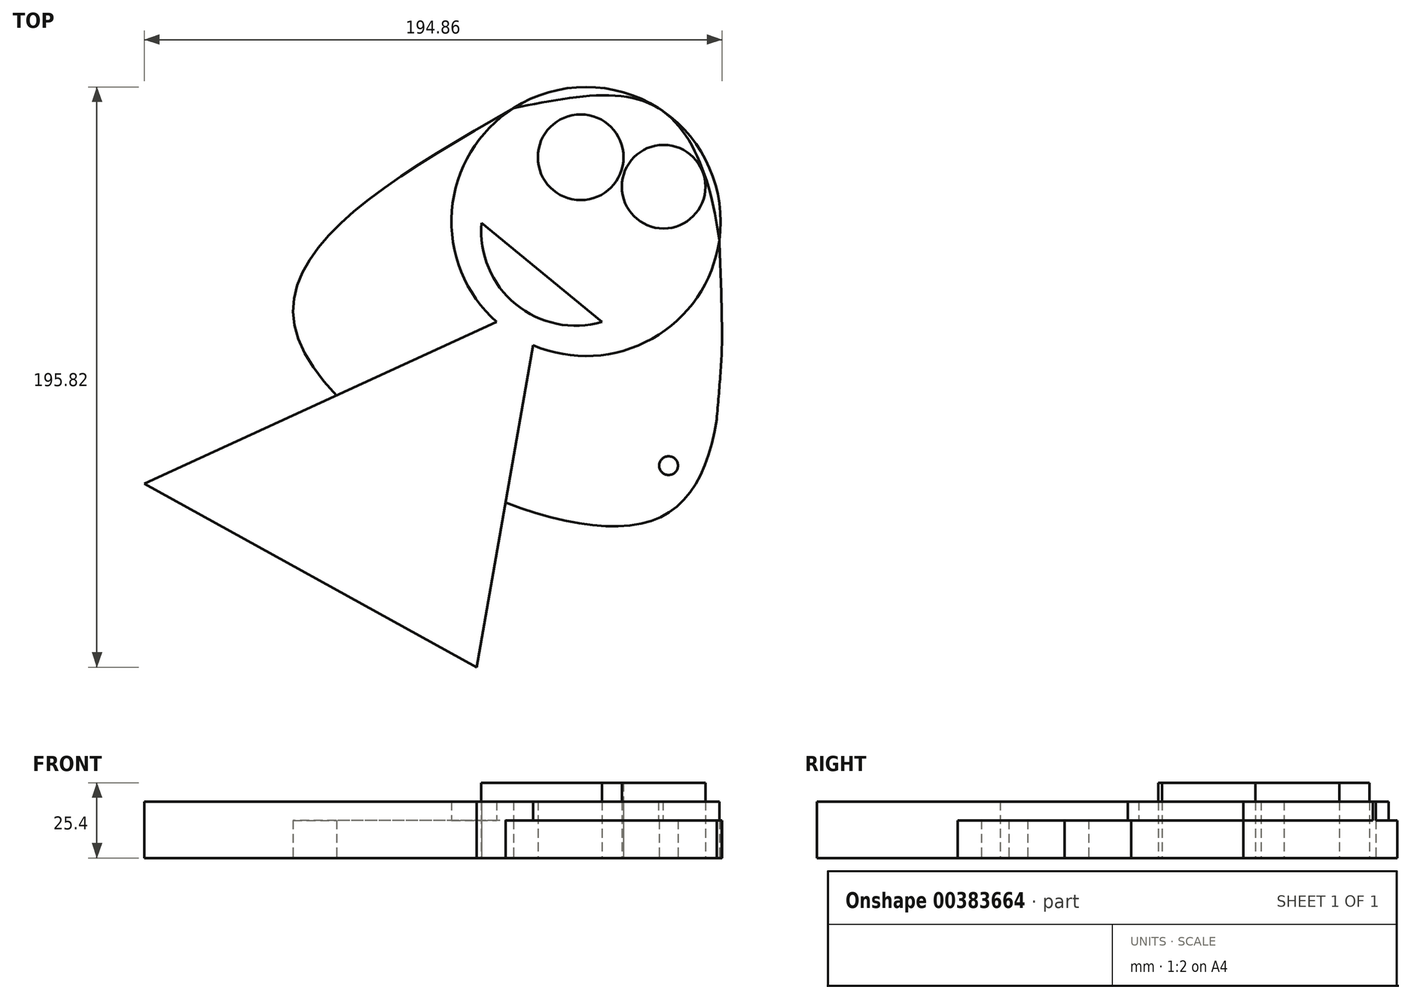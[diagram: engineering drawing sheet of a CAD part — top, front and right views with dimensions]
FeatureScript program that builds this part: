
annotation { "Feature Type Name" : "Feature", "Feature Type Description" : "" }
export const myFeature = defineFeature(function(context is Context, id is Id, definition is map)
    precondition{}
    {
        {
            var Q0;
            Q0=qCreatedBy(makeId("Top.planeOp"),FACE);
            var sketch = newSketch(context, id + "F0", { "sketchPlane" : qUnion([Q0])});
            skCircle(sketch, "E0", {"center": v(-79.47, 52.15) * mm, "radius": 45.4 * mm});
            skCircle(sketch, "E1", {"center": v(-81.27, 73.82) * mm, "radius": 14.46 * mm});
            skCircle(sketch, "E2", {"center": v(-53.28, 63.89) * mm, "radius": 14.1 * mm});
            skArc(sketch, "E3", {"start": v(-114.68, 51.7) * mm, "mid": v(-103.21, 24.23) * mm, "end": v(-74.05, 18.29) * mm});
            skFitSpline(sketch, "E4", {"points": [v(-103.93, 90.4) * mm, v(-177, 13.77) * mm, v(-59.15, -49.44) * mm, v(-34.52, 45.71) * mm], "startDerivative": vector(-381.58, -219.76) * mm, "endDerivative": vector(-17.69, 419.62) * mm});
            skFitSpline(sketch, "E5", {"points": [v(-103.93, 90.4) * mm, v(-55, 90.4) * mm, v(-34.52, 45.71) * mm, v(-35.4, -14.64) * mm], "startDerivative": vector(171.7, 34.93) * mm, "endDerivative": vector(-14.84, -167.93) * mm});
            skLineSegment(sketch, "E6", {"start": v(-109.63, 18.21) * mm, "end": v(-228.46, -36.35) * mm});
            skLineSegment(sketch, "E7", {"start": v(-228.46, -36.35) * mm, "end": v(-116.38, -98.26) * mm});
            skLineSegment(sketch, "E8", {"start": v(-116.38, -98.26) * mm, "end": v(-97.32, 10.4) * mm});
            skLineSegment(sketch, "E9", {"start": v(-74.05, 18.29) * mm, "end": v(-114.68, 51.7) * mm});
            skPoint(sketch, "E10", {"position": v(-58.61, 84.36) * mm});
            skPoint(sketch, "E11", {"position": v(-51.61, -30.25) * mm});
            skSolve(sketch);
        }
        {
            var Q0;
            Q0=makeQuery(id+"F0.imprint","IMPRINT",FACE,{"disambiguationData":[TD([[makeQuery(id+"F0.imprint","IMPRINT",EDGE,{"derivedFrom":sQuery(id+"F0.wireOp",EDGE,"E1")}),1.0]])]});
            var Q1;
            Q1=makeQuery(id+"F0.imprint","IMPRINT",FACE,{"disambiguationData":[TD([[makeQuery(id+"F0.imprint","IMPRINT",EDGE,{"derivedFrom":sQuery(id+"F0.wireOp",EDGE,"E2")}),1.0]])]});
            extrude(context, id + "F1", {"entities" : qUnion([Q0, Q1]), "depth" : 25.4 * mm});
        }
        {
            var Q0;
            Q0=makeQuery(id+"F0.imprint","IMPRINT",FACE,{"disambiguationData":[TD([[makeQuery(id+"F0.imprint","IMPRINT",EDGE,{"derivedFrom":sQuery(id+"F0.wireOp",EDGE,"E3")}),1.0]])]});
            extrude(context, id + "F2", {"entities" : qUnion([Q0]), "depth" : 25.4 * mm});
        }
        {
            var Q0;
            Q0=makeQuery(id+"F0.imprint","IMPRINT",FACE,{"disambiguationData":[TD([[makeQuery(id+"F0.imprint","IMPRINT",EDGE,{"derivedFrom":sQuery(id+"F0.wireOp",EDGE,"E1")}),-1.0]])]});
            var Q1;
            {var subQ5=sQuery(id+"F0.wireOp",EDGE,"E7");Q1=makeQuery(id+"F0.imprint","IMPRINT",FACE,{"disambiguationData":[TD([[makeQuery(id+"F0.imprint","IMPRINT",EDGE,{"derivedFrom":subQ5}),1.0]])]});}
            var Q2;
            {var subQ0=sQuery(id+"F0.wireOp",EDGE,"E6");var subQ1=sQuery(id+"F0.wireOp",EDGE,"E0");var subQ2=makeQuery(id+"F0.imprint","INTERSECT",VERTEX,{"derivedFrom":[subQ1,subQ0]});Q2=makeQuery(id+"F0.imprint","IMPRINT",FACE,{"disambiguationData":[TD([[makeQuery(id+"F0.imprint","IMPRINT",EDGE,{"disambiguationData":[TD([[subQ2,-1.0]])],"derivedFrom":subQ1}),-1.0]])]});}
            extrude(context, id + "F3", {"entities" : qUnion([Q0, Q1, Q2]), "depth" : 19.05 * mm});
        }
        {
            var Q0;
            {var subQ1=sQuery(id+"F0.wireOp",EDGE,"E0");var subQ3=sQuery(id+"F0.wireOp",EDGE,"E6");var subQ4=makeQuery(id+"F0.imprint","INTERSECT",VERTEX,{"derivedFrom":[subQ1,subQ3]});Q0=makeQuery(id+"F0.imprint","IMPRINT",FACE,{"disambiguationData":[TD([[makeQuery(id+"F0.imprint","IMPRINT",EDGE,{"disambiguationData":[TD([[subQ4,-1.0]])],"derivedFrom":subQ3}),-1.0]])]});}
            var Q1;
            {var subQ0=sQuery(id+"F0.wireOp",EDGE,"E5");var subQ1=sQuery(id+"F0.wireOp",EDGE,"E4");var subQ2=makeQuery(id+"F0.imprint","INTERSECT",VERTEX,{"disambiguationData":[OD(0.0)],"derivedFrom":[subQ1,subQ0]});Q1=makeQuery(id+"F0.imprint","IMPRINT",FACE,{"disambiguationData":[TD([[makeQuery(id+"F0.imprint","IMPRINT",EDGE,{"disambiguationData":[TD([[subQ2,1.0]])],"derivedFrom":subQ1}),1.0]])]});}
            var Q2;
            {var subQ0=sQuery(id+"F0.wireOp",EDGE,"E5");var subQ1=sQuery(id+"F0.wireOp",EDGE,"E0");var subQ3=makeQuery(id+"F0.imprint","INTERSECT",VERTEX,{"disambiguationData":[OD(1.0)],"derivedFrom":[subQ1,subQ0]});Q2=makeQuery(id+"F0.imprint","IMPRINT",FACE,{"disambiguationData":[TD([[makeQuery(id+"F0.imprint","IMPRINT",EDGE,{"disambiguationData":[TD([[subQ3,1.0]])],"derivedFrom":subQ1}),1.0]])]});}
            var Q3;
            {var subQ0=sQuery(id+"F0.wireOp",EDGE,"E5");var subQ1=sQuery(id+"F0.wireOp",EDGE,"E0");var subQ3=makeQuery(id+"F0.imprint","INTERSECT",VERTEX,{"disambiguationData":[OD(0.0)],"derivedFrom":[subQ1,subQ0]});Q3=makeQuery(id+"F0.imprint","IMPRINT",FACE,{"disambiguationData":[TD([[makeQuery(id+"F0.imprint","IMPRINT",EDGE,{"disambiguationData":[TD([[subQ3,-1.0]])],"derivedFrom":subQ1}),1.0]])]});}
            extrude(context, id + "F4", {"entities" : qUnion([Q0, Q1, Q2, Q3]), "operationType" : NewBodyOperationType.ADD, "depth" : 12.7 * mm});
        }
        {
            var Q0;
            Q0=sQuery(id+"F0.wireOp",VERTEX,"E11");
            var Q1;
            Q1=makeQuery(id+"F3.opExtrude","SWEPT_BODY",BODY,{"disambiguationData":[OSD([sQuery(id+"F0.wireOp",EDGE,"E0"),sQuery(id+"F0.wireOp",EDGE,"E1"),sQuery(id+"F0.wireOp",EDGE,"E2"),sQuery(id+"F0.wireOp",EDGE,"E3"),sQuery(id+"F0.wireOp",EDGE,"E5"),sQuery(id+"F0.wireOp",EDGE,"E6"),sQuery(id+"F0.wireOp",EDGE,"E7"),sQuery(id+"F0.wireOp",EDGE,"E8"),sQuery(id+"F0.wireOp",EDGE,"E9")])]});
            hole(context, id + "F5", {"style" : HoleStyle.SIMPLE, "endStyle" : HoleEndStyle.THROUGH, "oppositeDirection" : true, "holeDiameter" : 6.35 * mm, "isTappedThrough" : true, "tappedDepth" : 12.7 * mm, "tapClearance" : 3, "locations" : qUnion([Q0]), "scope" : qUnion([Q1])});
        }
    });
